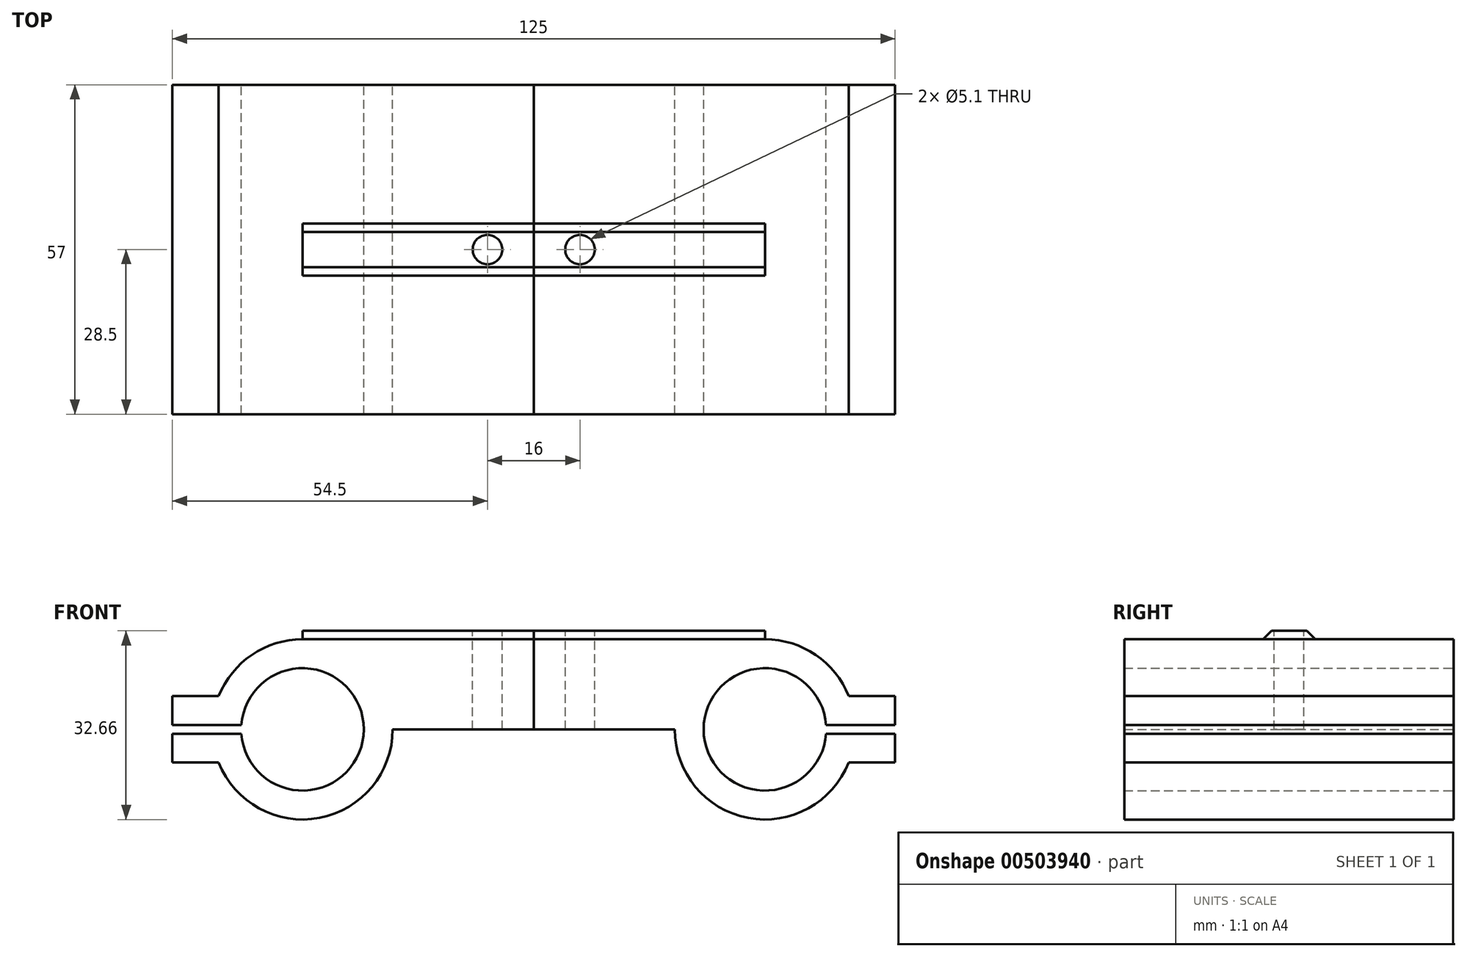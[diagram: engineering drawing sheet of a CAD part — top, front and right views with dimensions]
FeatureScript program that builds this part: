
annotation { "Feature Type Name" : "Feature", "Feature Type Description" : "" }
export const myFeature = defineFeature(function(context is Context, id is Id, definition is map)
    precondition{}
    {
        {
            var Q0;
            Q0=qCreatedBy(makeId("Front.planeOp"),FACE);
            var sketch = newSketch(context, id + "F0", { "sketchPlane" : qUnion([Q0])});
            skCircle(sketch, "E0", {"center": v(0, 0) * mm, "radius": 10.6 * mm});
            skCircle(sketch, "E1", {"center": v(0, 0) * mm, "radius": 15.6 * mm});
            skLineSegment(sketch, "E2", {"start": v(22.5, 5.75) * mm, "end": v(22.5, 0.75) * mm});
            skLineSegment(sketch, "E3", {"start": v(22.5, 0.75) * mm, "end": v(10.57, 0.75) * mm});
            skLineSegment(sketch, "E4", {"start": v(10.57, 0.75) * mm, "end": v(10.57, -0.75) * mm});
            skLineSegment(sketch, "E5", {"start": v(10.57, -0.75) * mm, "end": v(22.5, -0.75) * mm});
            skLineSegment(sketch, "E6", {"start": v(22.5, -0.75) * mm, "end": v(22.5, -5.75) * mm});
            skLineSegment(sketch, "E7", {"start": v(-63.04, 0) * mm, "end": v(52.32, 0) * mm, "construction": true});
            skLineSegment(sketch, "E8", {"start": v(22.5, 5.75) * mm, "end": v(14.5, 5.75) * mm});
            skLineSegment(sketch, "E9", {"start": v(22.5, -5.75) * mm, "end": v(14.5, -5.75) * mm});
            skLineSegment(sketch, "E10", {"start": v(0, 15.6) * mm, "end": v(-40, 15.6) * mm});
            skLineSegment(sketch, "E11", {"start": v(-40, 15.6) * mm, "end": v(-40, 0) * mm});
            skLineSegment(sketch, "E12", {"start": v(-40, 0) * mm, "end": v(-15.6, 0) * mm});
            skSolve(sketch);
        }
        {
            var Q0;
            {var subQ0=sQuery(id+"F0.wireOp",EDGE,"E10");Q0=makeQuery(id+"F0.imprint","IMPRINT",FACE,{"disambiguationData":[TD([[makeQuery(id+"F0.imprint","IMPRINT",EDGE,{"derivedFrom":subQ0}),1.0]])]});}
            var Q1;
            {var subQ0=sQuery(id+"F0.wireOp",EDGE,"E1");var subQ3=makeQuery(id+"F0.imprint","INTERSECT",VERTEX,{"derivedFrom":[subQ0,sQuery(id+"F0.wireOp",EDGE,"E8")]});Q1=makeQuery(id+"F0.imprint","IMPRINT",FACE,{"disambiguationData":[TD([[makeQuery(id+"F0.imprint","IMPRINT",EDGE,{"disambiguationData":[TD([[subQ3,1.0]])],"derivedFrom":subQ0}),1.0]])]});}
            var Q2;
            {var subQ4=sQuery(id+"F0.wireOp",EDGE,"E2");Q2=makeQuery(id+"F0.imprint","IMPRINT",FACE,{"disambiguationData":[TD([[makeQuery(id+"F0.imprint","IMPRINT",EDGE,{"derivedFrom":subQ4}),-1.0]])]});}
            var Q3;
            {var subQ4=sQuery(id+"F0.wireOp",EDGE,"E6");Q3=makeQuery(id+"F0.imprint","IMPRINT",FACE,{"disambiguationData":[TD([[makeQuery(id+"F0.imprint","IMPRINT",EDGE,{"derivedFrom":subQ4}),-1.0]])]});}
            extrude(context, id + "F1", {"entities" : qUnion([Q0, Q1, Q2, Q3]), "depth" : 57 * mm});
        }
        {
            var Q0;
            Q0=makeQuery(id+"F1.opExtrude","SWEPT_FACE",FACE,{"disambiguationData":[OSD([sQuery(id+"F0.wireOp",EDGE,"E11")])]});
            var sketch = newSketch(context, id + "F2", { "sketchPlane" : qUnion([Q0])});
            skLineSegment(sketch, "E13", {"start": v(24, 15.6) * mm, "end": v(25.45, 17.05) * mm});
            skLineSegment(sketch, "E14", {"start": v(25.45, 17.05) * mm, "end": v(31.55, 17.06) * mm});
            skLineSegment(sketch, "E15", {"start": v(31.55, 17.05) * mm, "end": v(33, 15.6) * mm});
            skLineSegment(sketch, "E16", {"start": v(28.5, 0) * mm, "end": v(28.5, 26.36) * mm, "construction": true});
            skSolve(sketch);
        }
        {
            var Q0;
            {var subQ0=sQuery(id+"F2.wireOp",EDGE,"E13");Q0=makeQuery(id+"F2.imprint","IMPRINT",FACE,{"disambiguationData":[TD([[makeQuery(id+"F2.imprint","IMPRINT",EDGE,{"derivedFrom":subQ0}),-1.0]])]});}
            extrude(context, id + "F3", {"entities" : qUnion([Q0]), "operationType" : NewBodyOperationType.ADD, "oppositeDirection" : true, "depth" : 40 * mm});
        }
        {
            var Q0;
            Q0=makeQuery(id+"F3.opExtrude","SWEPT_FACE",FACE,{"disambiguationData":[OSD([sQuery(id+"F2.wireOp",EDGE,"E14")])]});
            var sketch = newSketch(context, id + "F4", { "sketchPlane" : qUnion([Q0])});
            skCircle(sketch, "E17", {"center": v(-32, -28.5) * mm, "radius": 2.55 * mm});
            skPoint(sketch, "E17.centerSnap0", {"position": v(-40, -28.5) * mm});
            skSolve(sketch);
        }
        {
            var Q0;
            Q0=makeQuery(id+"F4.imprint","IMPRINT",FACE,{"disambiguationData":[TD([[makeQuery(id+"F4.imprint","IMPRINT",EDGE,{"derivedFrom":sQuery(id+"F4.wireOp",EDGE,"E17")}),1.0]])]});
            extrude(context, id + "F5", {"entities" : qUnion([Q0]), "operationType" : NewBodyOperationType.REMOVE, "endBound" : BoundingType.UP_TO_NEXT, "oppositeDirection" : true, "depth" : 25 * mm});
        }
        {
            var Q0;
            Q0=makeQuery(id+"F1.opExtrude","SWEPT_BODY",BODY,{"disambiguationData":[OSD([sQuery(id+"F0.wireOp",EDGE,"E0"),sQuery(id+"F0.wireOp",EDGE,"E1"),sQuery(id+"F0.wireOp",EDGE,"E2"),sQuery(id+"F0.wireOp",EDGE,"E3"),sQuery(id+"F0.wireOp",EDGE,"E5"),sQuery(id+"F0.wireOp",EDGE,"E6"),sQuery(id+"F0.wireOp",EDGE,"E8"),sQuery(id+"F0.wireOp",EDGE,"E9"),sQuery(id+"F0.wireOp",EDGE,"E10"),sQuery(id+"F0.wireOp",EDGE,"E11"),sQuery(id+"F0.wireOp",EDGE,"E12")])]});
            var Q1;
            {var subQ0=sQuery(id+"F0.wireOp",EDGE,"E11");Q1=makeQuery(id+"F3.boolean.opBoolean","MERGE",FACE,{"derivedFrom":[makeQuery(id+"F1.opExtrude","SWEPT_FACE",FACE,{"disambiguationData":[OSD([subQ0])]}),makeQuery(id+"F3.opExtrude","CAP_FACE",FACE,{"disambiguationData":[OSD([sQuery(id+"F0.wireOp",EDGE,"E10"),subQ0,sQuery(id+"F2.wireOp",EDGE,"E13"),sQuery(id+"F2.wireOp",EDGE,"E14"),sQuery(id+"F2.wireOp",EDGE,"E15")])],"isStart":true})]});}
            mirror(context, id + "F6", {"entities" : qUnion([Q0]), "mirrorPlane" : qUnion([Q1])});
        }
    });
